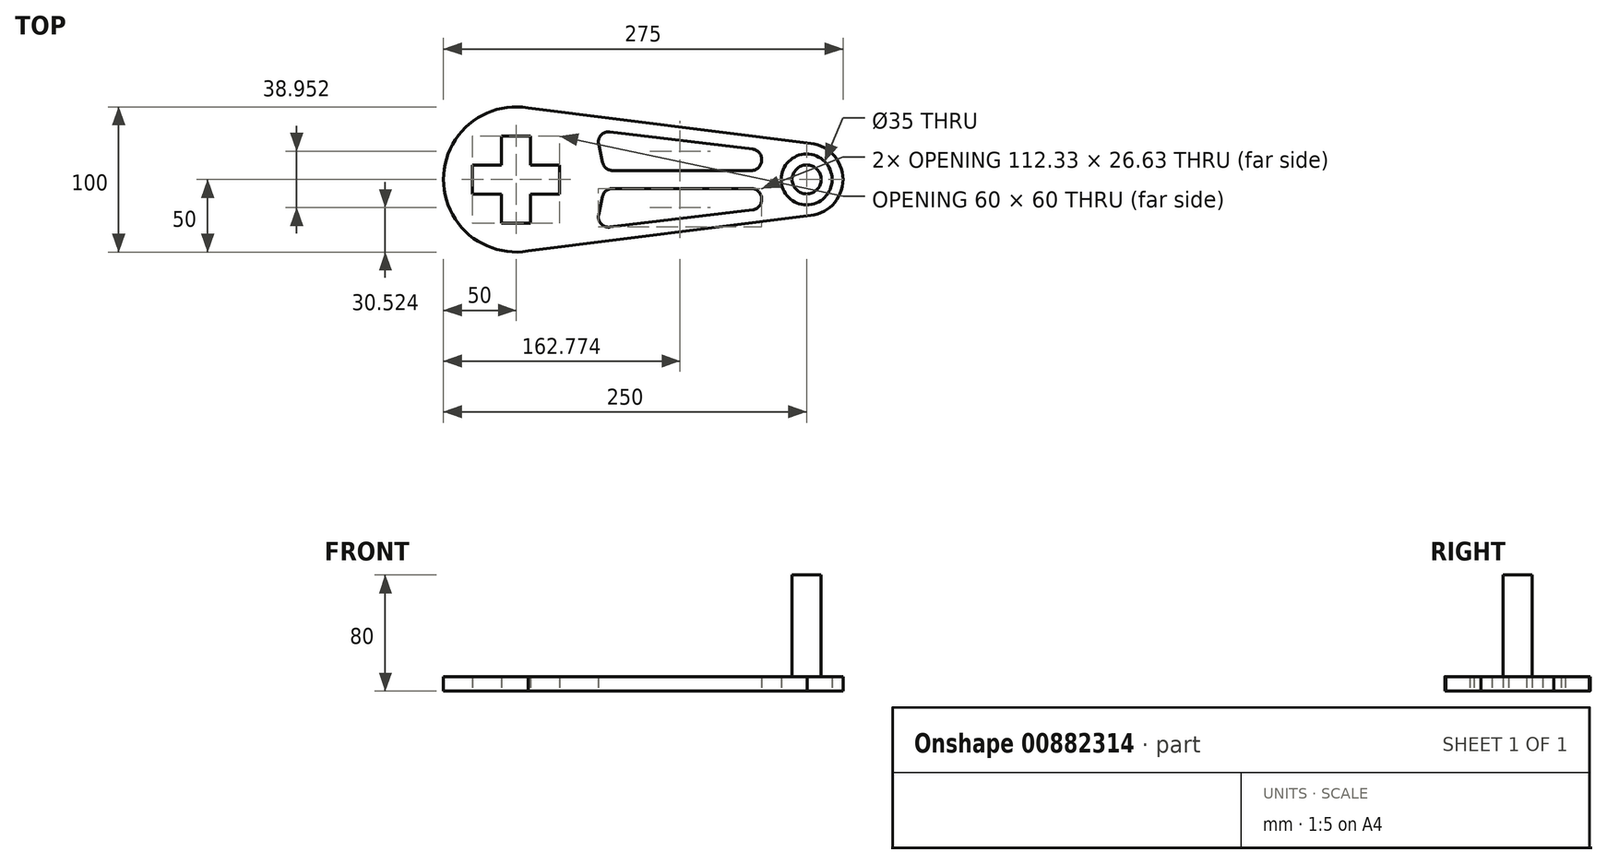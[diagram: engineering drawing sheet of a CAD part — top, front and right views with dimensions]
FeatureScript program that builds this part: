
annotation { "Feature Type Name" : "Feature", "Feature Type Description" : "" }
export const myFeature = defineFeature(function(context is Context, id is Id, definition is map)
    precondition{}
    {
        {
            var Q0;
            Q0=qCreatedBy(makeId("Top.planeOp"),FACE);
            var sketch = newSketch(context, id + "F0", { "sketchPlane" : qUnion([Q0])});
            skCircle(sketch, "E0", {"center": v(0, 0) * mm, "radius": 50 * mm});
            skLineSegment(sketch, "E1", {"start": v(0, 0) * mm, "end": v(0, 30) * mm, "construction": true});
            skLineSegment(sketch, "E2", {"start": v(0, 0) * mm, "end": v(-33.4, 0) * mm, "construction": true});
            skLineSegment(sketch, "E3", {"start": v(0, 30) * mm, "end": v(-10, 30) * mm});
            skLineSegment(sketch, "E4", {"start": v(-10, 30) * mm, "end": v(-10, 10) * mm});
            skLineSegment(sketch, "E5", {"start": v(-10, 10) * mm, "end": v(-30, 10) * mm});
            skLineSegment(sketch, "E6", {"start": v(-30, 10) * mm, "end": v(-30, 0) * mm});
            skLineSegment(sketch, "E7.MirrorCS", {"start": v(0, 30) * mm, "end": v(10, 30) * mm});
            skLineSegment(sketch, "E8.MirrorCS", {"start": v(10, 30) * mm, "end": v(10, 10) * mm});
            skLineSegment(sketch, "E9.MirrorCS", {"start": v(10, 10) * mm, "end": v(30, 10) * mm});
            skLineSegment(sketch, "E10.MirrorCS", {"start": v(30, 10) * mm, "end": v(30, 0) * mm});
            skLineSegment(sketch, "E11.MirrorCS", {"start": v(-30, -10) * mm, "end": v(-30, 0) * mm});
            skLineSegment(sketch, "E12.MirrorCS", {"start": v(-10, -10) * mm, "end": v(-30, -10) * mm});
            skLineSegment(sketch, "E13.MirrorCS", {"start": v(-10, -30) * mm, "end": v(-10, -10) * mm});
            skLineSegment(sketch, "E14.MirrorCS", {"start": v(0, -30) * mm, "end": v(-10, -30) * mm});
            skLineSegment(sketch, "E15.MirrorCS", {"start": v(0, -30) * mm, "end": v(10, -30) * mm});
            skLineSegment(sketch, "E16.MirrorCS", {"start": v(10, -30) * mm, "end": v(10, -10) * mm});
            skLineSegment(sketch, "E17.MirrorCS", {"start": v(10, -10) * mm, "end": v(30, -10) * mm});
            skLineSegment(sketch, "E18.MirrorCS", {"start": v(30, -10) * mm, "end": v(30, 0) * mm});
            skCircle(sketch, "E19", {"center": v(200, 0) * mm, "radius": 25 * mm});
            skLineSegment(sketch, "E20", {"start": v(8.22, 49.32) * mm, "end": v(200.26, 25) * mm});
            skLineSegment(sketch, "E21.MirrorCS", {"start": v(8.22, -49.32) * mm, "end": v(200.26, -25) * mm});
            skCircle(sketch, "E22", {"center": v(200, 0) * mm, "radius": 17.5 * mm});
            skLineSegment(sketch, "E23", {"start": v(56.77, 24.35) * mm, "end": v(59.53, 11.67) * mm});
            skLineSegment(sketch, "E24", {"start": v(66.37, 6.16) * mm, "end": v(161.94, 6.16) * mm});
            skLineSegment(sketch, "E25", {"start": v(168.94, 13.16) * mm, "end": v(168.94, 13.98) * mm});
            skLineSegment(sketch, "E26", {"start": v(162.78, 20.93) * mm, "end": v(64.44, 32.8) * mm});
            skPoint(sketch, "E27.visualSharp", {"position": v(54.67, 33.97) * mm});
            skArc(sketch, "E27.filletArc", {"start": v(64.44, 32.8) * mm, "mid": v(58.43, 30.55) * mm, "end": v(56.77, 24.35) * mm});
            skPoint(sketch, "E28.visualSharp", {"position": v(168.94, 20.2) * mm});
            skArc(sketch, "E28.filletArc", {"start": v(168.94, 13.98) * mm, "mid": v(167.18, 18.63) * mm, "end": v(162.78, 20.93) * mm});
            skPoint(sketch, "E29.visualSharp", {"position": v(168.94, 6.16) * mm});
            skArc(sketch, "E29.filletArc", {"start": v(161.94, 6.16) * mm, "mid": v(166.9, 8.21) * mm, "end": v(168.94, 13.16) * mm});
            skPoint(sketch, "E30.visualSharp", {"position": v(60.72, 6.16) * mm});
            skArc(sketch, "E30.filletArc", {"start": v(59.53, 11.67) * mm, "mid": v(61.97, 7.7) * mm, "end": v(66.37, 6.16) * mm});
            skLineSegment(sketch, "E31.MirrorCS", {"start": v(66.37, -6.16) * mm, "end": v(161.94, -6.16) * mm});
            skArc(sketch, "E32.MirrorCS", {"start": v(59.53, -11.67) * mm, "mid": v(61.97, -7.7) * mm, "end": v(66.37, -6.16) * mm});
            skLineSegment(sketch, "E33.MirrorCS", {"start": v(56.77, -24.35) * mm, "end": v(59.53, -11.67) * mm});
            skArc(sketch, "E34.MirrorCS", {"start": v(64.44, -32.8) * mm, "mid": v(58.43, -30.55) * mm, "end": v(56.77, -24.35) * mm});
            skLineSegment(sketch, "E35.MirrorCS", {"start": v(162.78, -20.93) * mm, "end": v(64.44, -32.8) * mm});
            skArc(sketch, "E36.MirrorCS", {"start": v(168.94, -13.98) * mm, "mid": v(167.18, -18.63) * mm, "end": v(162.78, -20.93) * mm});
            skLineSegment(sketch, "E37.MirrorCS", {"start": v(168.94, -13.16) * mm, "end": v(168.94, -13.98) * mm});
            skArc(sketch, "E38.MirrorCS", {"start": v(161.94, -6.16) * mm, "mid": v(166.9, -8.21) * mm, "end": v(168.94, -13.16) * mm});
            skSolve(sketch);
        }
        {
            var Q0;
            Q0=qSketchRegion(id+"F0",true);
            extrude(context, id + "F1", {"entities" : qUnion([Q0]), "depth" : 10 * mm, "offsetDistance" : 25 * mm});
        }
        {
            var Q0;
            Q0=makeQuery(id+"F1.opExtrude","CAP_FACE",FACE,{"disambiguationData":[OSD([sQuery(id+"F0.wireOp",EDGE,"E0"),sQuery(id+"F0.wireOp",EDGE,"E3"),sQuery(id+"F0.wireOp",EDGE,"E4"),sQuery(id+"F0.wireOp",EDGE,"E5"),sQuery(id+"F0.wireOp",EDGE,"E6"),sQuery(id+"F0.wireOp",EDGE,"E7.MirrorCS"),sQuery(id+"F0.wireOp",EDGE,"E8.MirrorCS"),sQuery(id+"F0.wireOp",EDGE,"E9.MirrorCS"),sQuery(id+"F0.wireOp",EDGE,"E10.MirrorCS"),sQuery(id+"F0.wireOp",EDGE,"E11.MirrorCS"),sQuery(id+"F0.wireOp",EDGE,"E12.MirrorCS"),sQuery(id+"F0.wireOp",EDGE,"E13.MirrorCS"),sQuery(id+"F0.wireOp",EDGE,"E14.MirrorCS"),sQuery(id+"F0.wireOp",EDGE,"E15.MirrorCS"),sQuery(id+"F0.wireOp",EDGE,"E16.MirrorCS"),sQuery(id+"F0.wireOp",EDGE,"E17.MirrorCS"),sQuery(id+"F0.wireOp",EDGE,"E18.MirrorCS"),sQuery(id+"F0.wireOp",EDGE,"E19"),sQuery(id+"F0.wireOp",EDGE,"E20"),sQuery(id+"F0.wireOp",EDGE,"E21.MirrorCS"),sQuery(id+"F0.wireOp",EDGE,"E22"),sQuery(id+"F0.wireOp",EDGE,"E23"),sQuery(id+"F0.wireOp",EDGE,"E24"),sQuery(id+"F0.wireOp",EDGE,"E25"),sQuery(id+"F0.wireOp",EDGE,"E26"),sQuery(id+"F0.wireOp",EDGE,"E27.filletArc"),sQuery(id+"F0.wireOp",EDGE,"E28.filletArc"),sQuery(id+"F0.wireOp",EDGE,"E29.filletArc"),sQuery(id+"F0.wireOp",EDGE,"E30.filletArc"),sQuery(id+"F0.wireOp",EDGE,"E31.MirrorCS"),sQuery(id+"F0.wireOp",EDGE,"E32.MirrorCS"),sQuery(id+"F0.wireOp",EDGE,"E33.MirrorCS"),sQuery(id+"F0.wireOp",EDGE,"E34.MirrorCS"),sQuery(id+"F0.wireOp",EDGE,"E35.MirrorCS"),sQuery(id+"F0.wireOp",EDGE,"E36.MirrorCS"),sQuery(id+"F0.wireOp",EDGE,"E37.MirrorCS"),sQuery(id+"F0.wireOp",EDGE,"E38.MirrorCS")])],"isStart":false});
            var sketch = newSketch(context, id + "F2", { "sketchPlane" : qUnion([Q0])});
            skCircle(sketch, "E39", {"center": v(200, 0) * mm, "radius": 10 * mm});
            skSolve(sketch);
        }
        {
            var Q0;
            Q0=qSketchRegion(id+"F2",true);
            extrude(context, id + "F3", {"entities" : qUnion([Q0]), "depth" : 70 * mm, "offsetDistance" : 25 * mm});
        }
    });
